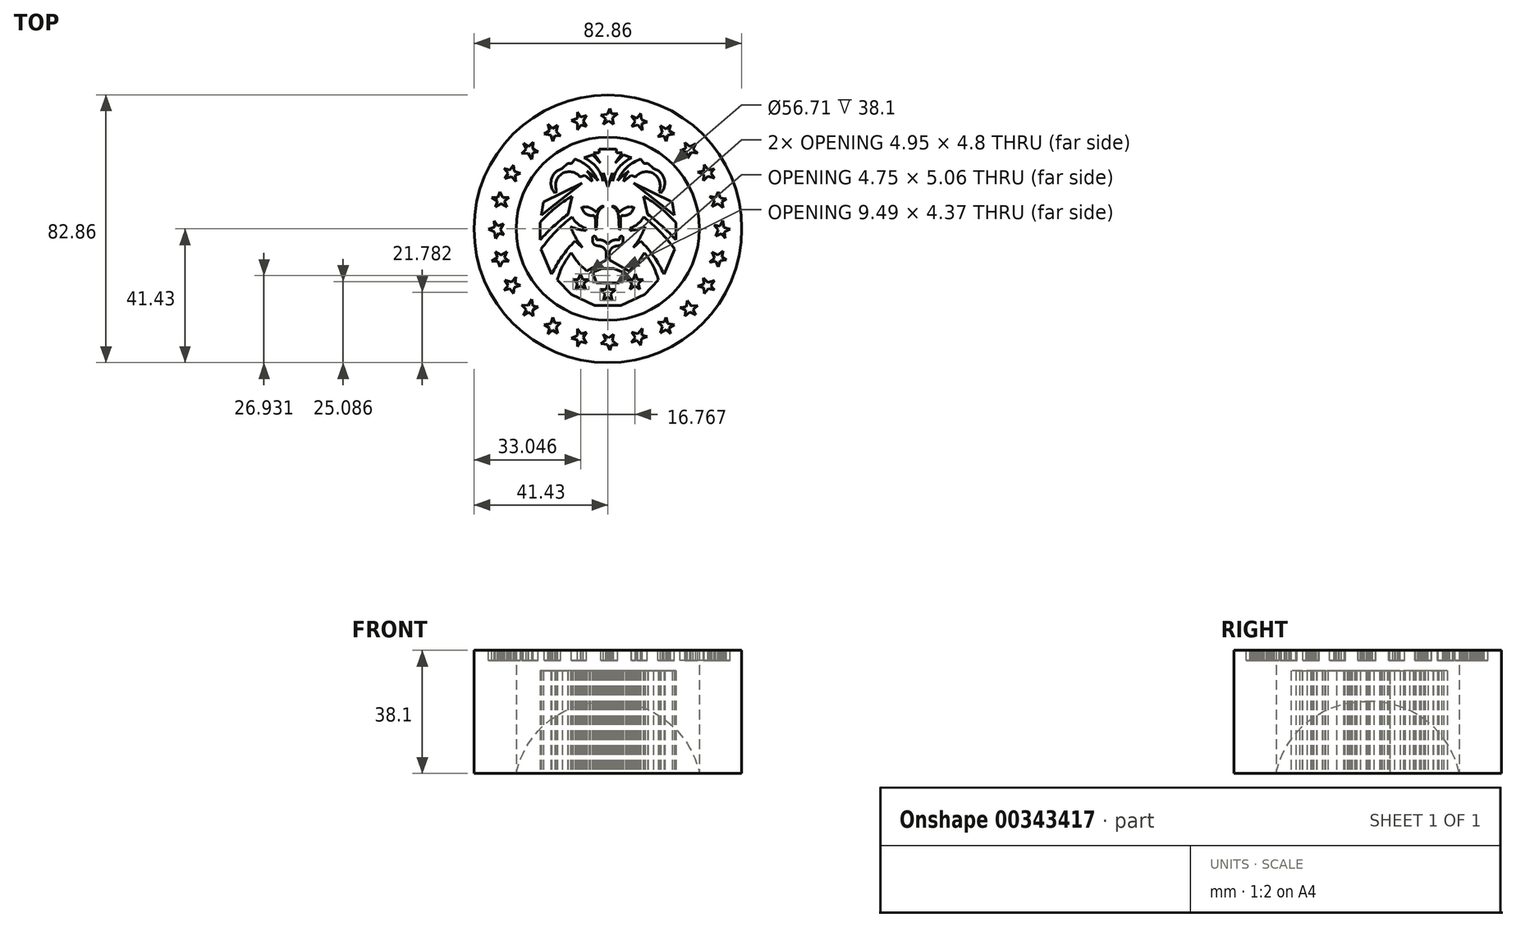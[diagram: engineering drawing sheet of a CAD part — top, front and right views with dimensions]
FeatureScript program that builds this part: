
annotation { "Feature Type Name" : "Feature", "Feature Type Description" : "" }
export const myFeature = defineFeature(function(context is Context, id is Id, definition is map)
    precondition{}
    {
        {
            var Q0;
            Q0=qCreatedBy(makeId("Top.planeOp"),FACE);
            var sketch = newSketch(context, id + "F0", { "sketchPlane" : qUnion([Q0])});
            skCircle(sketch, "E0", {"center": v(0, 0) * mm, "radius": 41.43 * mm});
            skCircle(sketch, "E1", {"center": v(0, 0) * mm, "radius": 28.35 * mm});
            skSolve(sketch);
        }
        {
            var Q0;
            Q0=qCreatedBy(makeId("Top.planeOp"),FACE);
            var sketch = newSketch(context, id + "F1", { "sketchPlane" : qUnion([Q0])});
            skLineSegment(sketch, "E2", {"start": v(0, 46.38) * mm, "end": v(0, -32.17) * mm});
            skSolve(sketch);
        }
        {
            var Q0;
            Q0=qCreatedBy(makeId("Top.planeOp"),FACE);
            var sketch = newSketch(context, id + "F2", { "sketchPlane" : qUnion([Q0])});
            skCircle(sketch, "E3", {"center": v(0, 0) * mm, "radius": 28.37 * mm});
            skSolve(sketch);
        }
        {
            var Q0;
            Q0=qCreatedBy(makeId("Top.planeOp"),FACE);
            var sketch = newSketch(context, id + "F3", { "sketchPlane" : qUnion([Q0])});
            skLineSegment(sketch, "E4", {"start": v(-11.03, 10.1) * mm, "end": v(-12.37, 4.51) * mm});
            skArc(sketch, "E5", {"start": v(-12.37, 4.51) * mm, "mid": v(-16.86, 0.72) * mm, "end": v(-21.02, -3.43) * mm});
            skLineSegment(sketch, "E6", {"start": v(-21.02, -3.43) * mm, "end": v(-21.02, 1.9) * mm});
            skArc(sketch, "E7", {"start": v(-11.03, 10.1) * mm, "mid": v(-16.36, 6.4) * mm, "end": v(-21.02, 1.9) * mm});
            skLineSegment(sketch, "E8", {"start": v(-8.04, 14.18) * mm, "end": v(-20.52, 4.22) * mm});
            skLineSegment(sketch, "E9", {"start": v(-20.52, 4.22) * mm, "end": v(-19.93, 8.27) * mm});
            skLineSegment(sketch, "E10", {"start": v(-19.93, 8.27) * mm, "end": v(-8.04, 14.18) * mm});
            skLineSegment(sketch, "E11", {"start": v(-17.38, -14.1) * mm, "end": v(-20.66, -6.3) * mm});
            skArc(sketch, "E12", {"start": v(-11.1, 3.65) * mm, "mid": v(-16.25, -0.98) * mm, "end": v(-20.66, -6.3) * mm});
            skArc(sketch, "E13", {"start": v(-11.1, 3.65) * mm, "mid": v(-9.28, 1.5) * mm, "end": v(-6.8, 0.15) * mm});
            skLineSegment(sketch, "E14", {"start": v(-6.8, 0.15) * mm, "end": v(-6.8, -0.48) * mm});
            skArc(sketch, "E15", {"start": v(-11.53, 0.68) * mm, "mid": v(-9.22, -0.13) * mm, "end": v(-6.8, -0.48) * mm});
            skArc(sketch, "E16", {"start": v(-11.53, 0.68) * mm, "mid": v(-9.97, -2.72) * mm, "end": v(-7.84, -5.8) * mm});
            skArc(sketch, "E17", {"start": v(-10.12, -3.78) * mm, "mid": v(-9, -4.81) * mm, "end": v(-7.84, -5.8) * mm});
            skArc(sketch, "E18", {"start": v(-10.12, -3.78) * mm, "mid": v(-14.22, -8.6) * mm, "end": v(-17.38, -14.1) * mm});
            skLineSegment(sketch, "E19", {"start": v(-3.6, -0.3) * mm, "end": v(-3.87, -0.1) * mm});
            skLineSegment(sketch, "E20", {"start": v(-3.87, -0.1) * mm, "end": v(-3.87, 2.84) * mm});
            skArc(sketch, "E21", {"start": v(-3.87, 2.84) * mm, "mid": v(-4, 3.55) * mm, "end": v(-4.34, 4.18) * mm});
            skArc(sketch, "E22", {"start": v(-7.84, 6.13) * mm, "mid": v(-6.5, 4.44) * mm, "end": v(-4.34, 4.18) * mm});
            skArc(sketch, "E23", {"start": v(-7.84, 6.13) * mm, "mid": v(-8.03, 6.34) * mm, "end": v(-8.3, 6.43) * mm});
            skArc(sketch, "E24", {"start": v(-5.4, 6.43) * mm, "mid": v(-6.85, 6.82) * mm, "end": v(-8.3, 6.43) * mm});
            skArc(sketch, "E25", {"start": v(-3.6, 5.13) * mm, "mid": v(-4.44, 5.87) * mm, "end": v(-5.4, 6.43) * mm});
            skFitSpline(sketch, "E26", {"points": [v(-3.6, 5.13) * mm, v(-3.38, 5.47) * mm, v(-3.2, 5.82) * mm, v(-2.82, 6.3) * mm, v(-2.41, 6.65) * mm, v(-1.95, 6.87) * mm, v(-1.78, 6.95) * mm, v(-1.2, 6.92) * mm], "startDerivative": vector(1.14, 2.33) * mm, "endDerivative": vector(4.24, -0.44) * mm});
            skArc(sketch, "E27", {"start": v(-1.2, 6.92) * mm, "mid": v(-2.6, 5.85) * mm, "end": v(-3.25, 4.2) * mm});
            skLineSegment(sketch, "E28", {"start": v(-3.25, 4.2) * mm, "end": v(-3.6, -0.3) * mm});
            skLineSegment(sketch, "E29", {"start": v(0, 24.6) * mm, "end": v(-2.68, 24.6) * mm});
            skLineSegment(sketch, "E30", {"start": v(-2.68, 24.6) * mm, "end": v(-2.68, 23.55) * mm});
            skLineSegment(sketch, "E31", {"start": v(-2.68, 23.55) * mm, "end": v(-4.43, 23.55) * mm});
            skLineSegment(sketch, "E32", {"start": v(-4.43, 23.55) * mm, "end": v(-2.25, 20.31) * mm});
            skLineSegment(sketch, "E33", {"start": v(-2.25, 20.31) * mm, "end": v(-4.76, 22.93) * mm});
            skLineSegment(sketch, "E34", {"start": v(-4.76, 22.93) * mm, "end": v(-7.41, 21.95) * mm});
            skArc(sketch, "E35", {"start": v(-1.52, 14.8) * mm, "mid": v(-3.57, 19.11) * mm, "end": v(-7.41, 21.95) * mm});
            skLineSegment(sketch, "E36", {"start": v(-1.52, 14.8) * mm, "end": v(-1.37, 17.25) * mm});
            skLineSegment(sketch, "E37", {"start": v(-1.37, 17.25) * mm, "end": v(0, 13) * mm});
            skLineSegment(sketch, "E38", {"start": v(0, 13) * mm, "end": v(0, 24.6) * mm});
            skLineSegment(sketch, "E39", {"start": v(-10.2, 21.56) * mm, "end": v(-11.2, 20.25) * mm});
            skLineSegment(sketch, "E40", {"start": v(-11.2, 20.25) * mm, "end": v(-12.45, 20.17) * mm});
            skLineSegment(sketch, "E41", {"start": v(-12.45, 20.17) * mm, "end": v(-14.05, 18.63) * mm});
            skArc(sketch, "E42", {"start": v(-14.05, 18.63) * mm, "mid": v(-17.41, 15.55) * mm, "end": v(-16.41, 11.1) * mm});
            skArc(sketch, "E43", {"start": v(-15.8, 11.64) * mm, "mid": v(-14.17, 17.04) * mm, "end": v(-8.61, 16.05) * mm});
            skLineSegment(sketch, "E44", {"start": v(-16.41, 11.1) * mm, "end": v(-15.8, 11.64) * mm});
            skLineSegment(sketch, "E45", {"start": v(-8.61, 16.05) * mm, "end": v(-7.18, 16.53) * mm});
            skLineSegment(sketch, "E46", {"start": v(-7.18, 16.53) * mm, "end": v(-4.87, 14.64) * mm});
            skArc(sketch, "E47", {"start": v(-4.87, 14.64) * mm, "mid": v(-5.43, 16.36) * mm, "end": v(-6.49, 17.82) * mm});
            skArc(sketch, "E48", {"start": v(-3.1, 14.92) * mm, "mid": v(-4.7, 16.46) * mm, "end": v(-6.49, 17.82) * mm});
            skArc(sketch, "E49", {"start": v(-3.1, 14.92) * mm, "mid": v(-5.9, 19.03) * mm, "end": v(-10.2, 21.56) * mm});
            skArc(sketch, "E50", {"start": v(0, -4.76) * mm, "mid": v(-1.62, -3.57) * mm, "end": v(-3.63, -3.45) * mm});
            skLineSegment(sketch, "E51", {"start": v(-3.63, -3.45) * mm, "end": v(-3.63, -2.82) * mm});
            skArc(sketch, "E52", {"start": v(-3.63, -2.82) * mm, "mid": v(-4.18, -2.26) * mm, "end": v(-4.74, -2.82) * mm});
            skLineSegment(sketch, "E53", {"start": v(-4.74, -2.82) * mm, "end": v(-4.74, -4.03) * mm});
            skArc(sketch, "E54", {"start": v(-4.74, -4.03) * mm, "mid": v(-4.04, -4.97) * mm, "end": v(-2.9, -5.27) * mm});
            skArc(sketch, "E55", {"start": v(-0.5, -7.1) * mm, "mid": v(-1.45, -5.86) * mm, "end": v(-2.9, -5.27) * mm});
            skLineSegment(sketch, "E56", {"start": v(-0.5, -7.1) * mm, "end": v(-0.5, -9.58) * mm});
            skLineSegment(sketch, "E57", {"start": v(-0.5, -9.58) * mm, "end": v(-6.45, -13.06) * mm});
            skArc(sketch, "E58", {"start": v(-11.28, -7.43) * mm, "mid": v(-9.16, -10.5) * mm, "end": v(-6.45, -13.06) * mm});
            skArc(sketch, "E59", {"start": v(-11.28, -7.43) * mm, "mid": v(-13.93, -11.4) * mm, "end": v(-15.65, -15.87) * mm});
            skLineSegment(sketch, "E60", {"start": v(-15.65, -15.87) * mm, "end": v(-11.37, -20.3) * mm});
            skLineSegment(sketch, "E61", {"start": v(-11.37, -20.3) * mm, "end": v(-4.05, -23.74) * mm});
            skLineSegment(sketch, "E62", {"start": v(-4.05, -23.74) * mm, "end": v(0, -23.74) * mm});
            skLineSegment(sketch, "E63", {"start": v(0, -23.74) * mm, "end": v(0, -21.12) * mm});
            skLineSegment(sketch, "E64", {"start": v(0, -21.12) * mm, "end": v(-1.36, -22.18) * mm});
            skLineSegment(sketch, "E65", {"start": v(-1.36, -22.18) * mm, "end": v(-0.9, -20.14) * mm});
            skLineSegment(sketch, "E66", {"start": v(-0.9, -20.14) * mm, "end": v(-2.38, -18.8) * mm});
            skLineSegment(sketch, "E67", {"start": v(-2.38, -18.8) * mm, "end": v(-0.55, -18.8) * mm});
            skLineSegment(sketch, "E68", {"start": v(-0.55, -18.8) * mm, "end": v(0, -17.12) * mm});
            skLineSegment(sketch, "E69", {"start": v(0, -17.12) * mm, "end": v(0, -16.68) * mm});
            skLineSegment(sketch, "E70", {"start": v(0, -16.68) * mm, "end": v(-3.54, -16.68) * mm});
            skLineSegment(sketch, "E71", {"start": v(-3.54, -16.68) * mm, "end": v(-4.74, -13.38) * mm});
            skLineSegment(sketch, "E72", {"start": v(-4.74, -13.38) * mm, "end": v(-1.8, -12.31) * mm});
            skLineSegment(sketch, "E73", {"start": v(-1.8, -12.31) * mm, "end": v(0, -12.31) * mm});
            skLineSegment(sketch, "E74", {"start": v(0, -12.31) * mm, "end": v(0, -4.76) * mm});
            skLineSegment(sketch, "E75", {"start": v(-8.46, -13.94) * mm, "end": v(-7.8, -15.72) * mm});
            skLineSegment(sketch, "E76", {"start": v(-7.8, -15.72) * mm, "end": v(-5.9, -15.72) * mm});
            skLineSegment(sketch, "E77", {"start": v(-5.9, -15.72) * mm, "end": v(-7.47, -16.87) * mm});
            skLineSegment(sketch, "E78", {"start": v(-7.47, -16.87) * mm, "end": v(-6.9, -18.73) * mm});
            skLineSegment(sketch, "E79", {"start": v(-6.9, -18.73) * mm, "end": v(-8.39, -17.6) * mm});
            skLineSegment(sketch, "E80", {"start": v(-8.39, -17.6) * mm, "end": v(-9.9, -18.74) * mm});
            skLineSegment(sketch, "E81", {"start": v(-9.9, -18.74) * mm, "end": v(-9.35, -16.93) * mm});
            skLineSegment(sketch, "E82", {"start": v(-9.35, -16.93) * mm, "end": v(-10.86, -15.77) * mm});
            skLineSegment(sketch, "E83", {"start": v(-10.86, -15.77) * mm, "end": v(-9.12, -15.77) * mm});
            skLineSegment(sketch, "E84", {"start": v(-9.12, -15.77) * mm, "end": v(-8.46, -13.94) * mm});
            skLineSegment(sketch, "E85.MirrorCS", {"start": v(0, 24.6) * mm, "end": v(2.68, 24.6) * mm});
            skLineSegment(sketch, "E86.MirrorCS", {"start": v(2.68, 24.6) * mm, "end": v(2.68, 23.55) * mm});
            skLineSegment(sketch, "E87.MirrorCS", {"start": v(2.68, 23.55) * mm, "end": v(4.43, 23.55) * mm});
            skLineSegment(sketch, "E88.MirrorCS", {"start": v(4.43, 23.55) * mm, "end": v(2.25, 20.31) * mm});
            skLineSegment(sketch, "E89.MirrorCS", {"start": v(2.25, 20.31) * mm, "end": v(4.76, 22.93) * mm});
            skLineSegment(sketch, "E90.MirrorCS", {"start": v(4.76, 22.93) * mm, "end": v(7.41, 21.95) * mm});
            skArc(sketch, "E91.MirrorCS", {"start": v(1.52, 14.8) * mm, "mid": v(3.57, 19.11) * mm, "end": v(7.41, 21.95) * mm});
            skLineSegment(sketch, "E92.MirrorCS", {"start": v(1.52, 14.8) * mm, "end": v(1.37, 17.25) * mm});
            skLineSegment(sketch, "E93.MirrorCS", {"start": v(1.37, 17.25) * mm, "end": v(0, 13) * mm});
            skArc(sketch, "E94.MirrorCS", {"start": v(3.1, 14.92) * mm, "mid": v(5.9, 19.03) * mm, "end": v(10.2, 21.56) * mm});
            skLineSegment(sketch, "E95.MirrorCS", {"start": v(10.2, 21.56) * mm, "end": v(11.2, 20.25) * mm});
            skLineSegment(sketch, "E96.MirrorCS", {"start": v(11.2, 20.25) * mm, "end": v(12.45, 20.17) * mm});
            skLineSegment(sketch, "E97.MirrorCS", {"start": v(12.45, 20.17) * mm, "end": v(14.05, 18.63) * mm});
            skArc(sketch, "E98.MirrorCS", {"start": v(14.05, 18.63) * mm, "mid": v(17.41, 15.55) * mm, "end": v(16.41, 11.1) * mm});
            skLineSegment(sketch, "E99.MirrorCS", {"start": v(16.41, 11.1) * mm, "end": v(15.8, 11.64) * mm});
            skArc(sketch, "E100.MirrorCS", {"start": v(15.8, 11.64) * mm, "mid": v(14.17, 17.04) * mm, "end": v(8.61, 16.05) * mm});
            skLineSegment(sketch, "E101.MirrorCS", {"start": v(8.61, 16.05) * mm, "end": v(7.18, 16.53) * mm});
            skLineSegment(sketch, "E102.MirrorCS", {"start": v(7.18, 16.53) * mm, "end": v(4.87, 14.64) * mm});
            skArc(sketch, "E103.MirrorCS", {"start": v(4.87, 14.64) * mm, "mid": v(5.43, 16.36) * mm, "end": v(6.49, 17.82) * mm});
            skArc(sketch, "E104.MirrorCS", {"start": v(3.1, 14.92) * mm, "mid": v(4.7, 16.46) * mm, "end": v(6.49, 17.82) * mm});
            skLineSegment(sketch, "E105.MirrorCS", {"start": v(19.93, 8.27) * mm, "end": v(8.04, 14.18) * mm});
            skLineSegment(sketch, "E106.MirrorCS", {"start": v(20.52, 4.22) * mm, "end": v(19.93, 8.27) * mm});
            skLineSegment(sketch, "E107.MirrorCS", {"start": v(8.04, 14.18) * mm, "end": v(20.52, 4.22) * mm});
            skLineSegment(sketch, "E108.MirrorCS", {"start": v(11.03, 10.1) * mm, "end": v(12.37, 4.51) * mm});
            skArc(sketch, "E109.MirrorCS", {"start": v(11.03, 10.1) * mm, "mid": v(16.36, 6.4) * mm, "end": v(21.02, 1.9) * mm});
            skLineSegment(sketch, "E110.MirrorCS", {"start": v(21.02, -3.43) * mm, "end": v(21.02, 1.9) * mm});
            skArc(sketch, "E111.MirrorCS", {"start": v(12.37, 4.51) * mm, "mid": v(16.86, 0.72) * mm, "end": v(21.02, -3.43) * mm});
            skArc(sketch, "E112.MirrorCS", {"start": v(11.1, 3.65) * mm, "mid": v(9.28, 1.5) * mm, "end": v(6.8, 0.15) * mm});
            skArc(sketch, "E113.MirrorCS", {"start": v(11.1, 3.65) * mm, "mid": v(16.25, -0.98) * mm, "end": v(20.66, -6.3) * mm});
            skLineSegment(sketch, "E114.MirrorCS", {"start": v(17.38, -14.1) * mm, "end": v(20.66, -6.3) * mm});
            skArc(sketch, "E115.MirrorCS", {"start": v(10.12, -3.78) * mm, "mid": v(14.22, -8.6) * mm, "end": v(17.38, -14.1) * mm});
            skArc(sketch, "E116.MirrorCS", {"start": v(10.12, -3.78) * mm, "mid": v(9, -4.81) * mm, "end": v(7.84, -5.8) * mm});
            skArc(sketch, "E117.MirrorCS", {"start": v(11.53, 0.68) * mm, "mid": v(9.97, -2.72) * mm, "end": v(7.84, -5.8) * mm});
            skArc(sketch, "E118.MirrorCS", {"start": v(11.53, 0.68) * mm, "mid": v(9.22, -0.13) * mm, "end": v(6.8, -0.48) * mm});
            skLineSegment(sketch, "E119.MirrorCS", {"start": v(6.8, 0.15) * mm, "end": v(6.8, -0.48) * mm});
            skFitSpline(sketch, "E120.MirrorCS", {"points": [v(3.6, 5.13) * mm, v(3.38, 5.47) * mm, v(3.2, 5.82) * mm, v(2.82, 6.3) * mm, v(2.41, 6.65) * mm, v(1.95, 6.87) * mm, v(1.78, 6.95) * mm, v(1.2, 6.92) * mm], "startDerivative": vector(-1.14, 2.33) * mm, "endDerivative": vector(-4.24, -0.44) * mm});
            skArc(sketch, "E121.MirrorCS", {"start": v(3.6, 5.13) * mm, "mid": v(4.44, 5.87) * mm, "end": v(5.4, 6.43) * mm});
            skArc(sketch, "E122.MirrorCS", {"start": v(5.4, 6.43) * mm, "mid": v(6.85, 6.82) * mm, "end": v(8.3, 6.43) * mm});
            skArc(sketch, "E123.MirrorCS", {"start": v(7.84, 6.13) * mm, "mid": v(8.03, 6.34) * mm, "end": v(8.3, 6.43) * mm});
            skArc(sketch, "E124.MirrorCS", {"start": v(7.84, 6.13) * mm, "mid": v(6.5, 4.44) * mm, "end": v(4.34, 4.18) * mm});
            skArc(sketch, "E125.MirrorCS", {"start": v(3.87, 2.84) * mm, "mid": v(4, 3.55) * mm, "end": v(4.34, 4.18) * mm});
            skLineSegment(sketch, "E126.MirrorCS", {"start": v(3.87, -0.1) * mm, "end": v(3.87, 2.84) * mm});
            skLineSegment(sketch, "E127.MirrorCS", {"start": v(3.6, -0.3) * mm, "end": v(3.87, -0.1) * mm});
            skLineSegment(sketch, "E128.MirrorCS", {"start": v(3.25, 4.2) * mm, "end": v(3.6, -0.3) * mm});
            skArc(sketch, "E129.MirrorCS", {"start": v(1.2, 6.92) * mm, "mid": v(2.6, 5.85) * mm, "end": v(3.25, 4.2) * mm});
            skArc(sketch, "E130.MirrorCS", {"start": v(0, -4.76) * mm, "mid": v(1.62, -3.57) * mm, "end": v(3.63, -3.45) * mm});
            skLineSegment(sketch, "E131.MirrorCS", {"start": v(3.63, -3.45) * mm, "end": v(3.63, -2.82) * mm});
            skArc(sketch, "E132.MirrorCS", {"start": v(3.63, -2.82) * mm, "mid": v(4.18, -2.26) * mm, "end": v(4.74, -2.82) * mm});
            skLineSegment(sketch, "E133.MirrorCS", {"start": v(4.74, -2.82) * mm, "end": v(4.74, -4.03) * mm});
            skArc(sketch, "E134.MirrorCS", {"start": v(4.74, -4.03) * mm, "mid": v(4.04, -4.97) * mm, "end": v(2.9, -5.27) * mm});
            skArc(sketch, "E135.MirrorCS", {"start": v(0.5, -7.1) * mm, "mid": v(1.45, -5.86) * mm, "end": v(2.9, -5.27) * mm});
            skLineSegment(sketch, "E136.MirrorCS", {"start": v(0.5, -7.1) * mm, "end": v(0.5, -9.58) * mm});
            skLineSegment(sketch, "E137.MirrorCS", {"start": v(0.5, -9.58) * mm, "end": v(6.45, -13.06) * mm});
            skArc(sketch, "E138.MirrorCS", {"start": v(11.28, -7.43) * mm, "mid": v(9.16, -10.5) * mm, "end": v(6.45, -13.06) * mm});
            skArc(sketch, "E139.MirrorCS", {"start": v(11.28, -7.43) * mm, "mid": v(13.93, -11.4) * mm, "end": v(15.65, -15.87) * mm});
            skLineSegment(sketch, "E140.MirrorCS", {"start": v(15.65, -15.87) * mm, "end": v(11.37, -20.3) * mm});
            skLineSegment(sketch, "E141.MirrorCS", {"start": v(11.37, -20.3) * mm, "end": v(4.05, -23.74) * mm});
            skLineSegment(sketch, "E142.MirrorCS", {"start": v(4.05, -23.74) * mm, "end": v(0, -23.74) * mm});
            skLineSegment(sketch, "E143.MirrorCS", {"start": v(0, -21.12) * mm, "end": v(1.36, -22.18) * mm});
            skLineSegment(sketch, "E144.MirrorCS", {"start": v(1.36, -22.18) * mm, "end": v(0.9, -20.14) * mm});
            skLineSegment(sketch, "E145.MirrorCS", {"start": v(0.9, -20.14) * mm, "end": v(2.38, -18.8) * mm});
            skLineSegment(sketch, "E146.MirrorCS", {"start": v(2.38, -18.8) * mm, "end": v(0.55, -18.8) * mm});
            skLineSegment(sketch, "E147.MirrorCS", {"start": v(0.55, -18.8) * mm, "end": v(0, -17.12) * mm});
            skLineSegment(sketch, "E148.MirrorCS", {"start": v(0, -16.68) * mm, "end": v(3.54, -16.68) * mm});
            skLineSegment(sketch, "E149.MirrorCS", {"start": v(3.54, -16.68) * mm, "end": v(4.74, -13.38) * mm});
            skLineSegment(sketch, "E150.MirrorCS", {"start": v(4.74, -13.38) * mm, "end": v(1.8, -12.31) * mm});
            skLineSegment(sketch, "E151.MirrorCS", {"start": v(1.8, -12.31) * mm, "end": v(0, -12.31) * mm});
            skLineSegment(sketch, "E152.MirrorCS", {"start": v(9.12, -15.77) * mm, "end": v(8.46, -13.94) * mm});
            skLineSegment(sketch, "E153.MirrorCS", {"start": v(10.86, -15.77) * mm, "end": v(9.12, -15.77) * mm});
            skLineSegment(sketch, "E154.MirrorCS", {"start": v(9.35, -16.93) * mm, "end": v(10.86, -15.77) * mm});
            skLineSegment(sketch, "E155.MirrorCS", {"start": v(9.9, -18.74) * mm, "end": v(9.35, -16.93) * mm});
            skLineSegment(sketch, "E156.MirrorCS", {"start": v(8.39, -17.6) * mm, "end": v(9.9, -18.74) * mm});
            skLineSegment(sketch, "E157.MirrorCS", {"start": v(6.9, -18.73) * mm, "end": v(8.39, -17.6) * mm});
            skLineSegment(sketch, "E158.MirrorCS", {"start": v(7.47, -16.87) * mm, "end": v(6.9, -18.73) * mm});
            skLineSegment(sketch, "E159.MirrorCS", {"start": v(5.9, -15.72) * mm, "end": v(7.47, -16.87) * mm});
            skLineSegment(sketch, "E160.MirrorCS", {"start": v(7.8, -15.72) * mm, "end": v(5.9, -15.72) * mm});
            skLineSegment(sketch, "E161.MirrorCS", {"start": v(8.46, -13.94) * mm, "end": v(7.8, -15.72) * mm});
            skSolve(sketch);
        }
        {
            var Q0;
            Q0=makeQuery(id+"F0.imprint","IMPRINT",FACE,{"disambiguationData":[TD([[makeQuery(id+"F0.imprint","IMPRINT",EDGE,{"derivedFrom":sQuery(id+"F0.wireOp",EDGE,"E0")}),1.0]])]});
            extrude(context, id + "F4", {"entities" : qUnion([Q0]), "depth" : 38.1 * mm});
        }
        {
            var Q0;
            Q0=makeQuery(id+"F4.opExtrude","CAP_FACE",FACE,{"disambiguationData":[OSD([sQuery(id+"F0.wireOp",EDGE,"E0"),sQuery(id+"F0.wireOp",EDGE,"E1")])],"isStart":false});
            var sketch = newSketch(context, id + "F5", { "sketchPlane" : qUnion([Q0])});
            skLineSegment(sketch, "E162", {"start": v(-33.47, 11.5) * mm, "end": v(-32.57, 9.68) * mm});
            skLineSegment(sketch, "E163", {"start": v(-32.57, 9.68) * mm, "end": v(-30.6, 9.68) * mm});
            skLineSegment(sketch, "E164", {"start": v(-30.6, 9.68) * mm, "end": v(-31.95, 8.6) * mm});
            skLineSegment(sketch, "E165", {"start": v(-31.95, 8.6) * mm, "end": v(-31.22, 6.78) * mm});
            skLineSegment(sketch, "E166", {"start": v(-31.22, 6.78) * mm, "end": v(-33.02, 7.83) * mm});
            skLineSegment(sketch, "E167", {"start": v(-33.02, 7.83) * mm, "end": v(-34.75, 6.72) * mm});
            skLineSegment(sketch, "E168", {"start": v(-34.75, 6.72) * mm, "end": v(-34.23, 8.6) * mm});
            skLineSegment(sketch, "E169", {"start": v(-34.23, 8.6) * mm, "end": v(-35.9, 9.68) * mm});
            skLineSegment(sketch, "E170", {"start": v(-35.9, 9.68) * mm, "end": v(-34, 9.68) * mm});
            skLineSegment(sketch, "E171", {"start": v(-34, 9.68) * mm, "end": v(-33.47, 11.5) * mm});
            skLineSegment(sketch, "E172", {"start": v(-29.26, 19.74) * mm, "end": v(-28.93, 17.74) * mm});
            skLineSegment(sketch, "E173", {"start": v(-28.93, 17.74) * mm, "end": v(-27.04, 17.16) * mm});
            skLineSegment(sketch, "E174", {"start": v(-27.04, 17.16) * mm, "end": v(-28.65, 16.52) * mm});
            skLineSegment(sketch, "E175", {"start": v(-28.65, 16.52) * mm, "end": v(-28.49, 14.57) * mm});
            skLineSegment(sketch, "E176", {"start": v(-28.49, 14.57) * mm, "end": v(-29.9, 16.1) * mm});
            skLineSegment(sketch, "E177", {"start": v(-29.9, 16.1) * mm, "end": v(-31.88, 15.55) * mm});
            skLineSegment(sketch, "E178", {"start": v(-31.88, 15.55) * mm, "end": v(-30.83, 17.19) * mm});
            skLineSegment(sketch, "E179", {"start": v(-30.83, 17.19) * mm, "end": v(-32.12, 18.72) * mm});
            skLineSegment(sketch, "E180", {"start": v(-32.12, 18.72) * mm, "end": v(-30.3, 18.16) * mm});
            skLineSegment(sketch, "E181", {"start": v(-30.3, 18.16) * mm, "end": v(-29.26, 19.74) * mm});
            skLineSegment(sketch, "E182.0", {"start": v(-32.12, 18.72) * mm, "end": v(-28.93, 17.74) * mm, "construction": true});
            skLineSegment(sketch, "E183.0", {"start": v(-30.83, 17.19) * mm, "end": v(-28.65, 16.52) * mm, "construction": true});
            skLineSegment(sketch, "E184", {"start": v(-23.14, 26.76) * mm, "end": v(-23.26, 24.73) * mm});
            skLineSegment(sketch, "E185", {"start": v(-23.26, 24.73) * mm, "end": v(-21.56, 23.74) * mm});
            skLineSegment(sketch, "E186", {"start": v(-21.56, 23.74) * mm, "end": v(-23.27, 23.48) * mm});
            skLineSegment(sketch, "E187", {"start": v(-23.27, 23.48) * mm, "end": v(-23.55, 21.54) * mm});
            skLineSegment(sketch, "E188", {"start": v(-23.55, 21.54) * mm, "end": v(-24.58, 23.35) * mm});
            skLineSegment(sketch, "E189", {"start": v(-24.58, 23.35) * mm, "end": v(-26.64, 23.25) * mm});
            skLineSegment(sketch, "E190", {"start": v(-26.64, 23.25) * mm, "end": v(-25.25, 24.62) * mm});
            skLineSegment(sketch, "E191", {"start": v(-25.25, 24.62) * mm, "end": v(-26.16, 26.4) * mm});
            skLineSegment(sketch, "E192", {"start": v(-26.16, 26.4) * mm, "end": v(-24.51, 25.45) * mm});
            skLineSegment(sketch, "E193", {"start": v(-24.51, 25.45) * mm, "end": v(-23.14, 26.76) * mm});
            skLineSegment(sketch, "E194.0", {"start": v(-26.16, 26.4) * mm, "end": v(-23.26, 24.73) * mm, "construction": true});
            skLineSegment(sketch, "E195.0", {"start": v(-25.25, 24.62) * mm, "end": v(-23.27, 23.48) * mm, "construction": true});
            skLineSegment(sketch, "E196", {"start": v(-15.5, 32.04) * mm, "end": v(-16.06, 30.09) * mm});
            skLineSegment(sketch, "E197", {"start": v(-16.06, 30.09) * mm, "end": v(-14.6, 28.76) * mm});
            skLineSegment(sketch, "E198", {"start": v(-14.6, 28.76) * mm, "end": v(-16.33, 28.86) * mm});
            skLineSegment(sketch, "E199", {"start": v(-16.33, 28.86) * mm, "end": v(-17.02, 27.04) * mm});
            skLineSegment(sketch, "E200", {"start": v(-17.02, 27.04) * mm, "end": v(-17.64, 29.02) * mm});
            skLineSegment(sketch, "E201", {"start": v(-17.64, 29.02) * mm, "end": v(-19.67, 29.37) * mm});
            skLineSegment(sketch, "E202", {"start": v(-19.67, 29.37) * mm, "end": v(-18.02, 30.4) * mm});
            skLineSegment(sketch, "E203", {"start": v(-18.02, 30.4) * mm, "end": v(-18.52, 32.34) * mm});
            skLineSegment(sketch, "E204", {"start": v(-18.52, 32.34) * mm, "end": v(-17.12, 31.06) * mm});
            skLineSegment(sketch, "E205", {"start": v(-17.12, 31.06) * mm, "end": v(-15.5, 32.04) * mm});
            skLineSegment(sketch, "E206.0", {"start": v(-18.02, 30.4) * mm, "end": v(-16.33, 28.86) * mm, "construction": true});
            skLineSegment(sketch, "E207.0", {"start": v(-18.52, 32.34) * mm, "end": v(-16.06, 30.09) * mm, "construction": true});
            skLineSegment(sketch, "E208", {"start": v(-6.6, 35.04) * mm, "end": v(-7.65, 33.3) * mm});
            skLineSegment(sketch, "E209", {"start": v(-7.65, 33.3) * mm, "end": v(-6.6, 31.63) * mm});
            skLineSegment(sketch, "E210", {"start": v(-6.6, 31.63) * mm, "end": v(-8.24, 32.2) * mm});
            skLineSegment(sketch, "E211", {"start": v(-8.24, 32.2) * mm, "end": v(-9.38, 30.61) * mm});
            skLineSegment(sketch, "E212", {"start": v(-9.38, 30.61) * mm, "end": v(-9.46, 32.69) * mm});
            skLineSegment(sketch, "E213", {"start": v(-9.46, 32.69) * mm, "end": v(-11.32, 33.56) * mm});
            skLineSegment(sketch, "E214", {"start": v(-11.32, 33.56) * mm, "end": v(-9.46, 34.12) * mm});
            skLineSegment(sketch, "E215", {"start": v(-9.46, 34.12) * mm, "end": v(-9.43, 36.12) * mm});
            skLineSegment(sketch, "E216", {"start": v(-9.43, 36.12) * mm, "end": v(-8.42, 34.51) * mm});
            skLineSegment(sketch, "E217", {"start": v(-8.42, 34.51) * mm, "end": v(-6.6, 35.04) * mm});
            skLineSegment(sketch, "E218.0", {"start": v(-9.43, 36.12) * mm, "end": v(-7.65, 33.3) * mm, "construction": true});
            skLineSegment(sketch, "E219.0", {"start": v(-9.46, 34.12) * mm, "end": v(-8.24, 32.2) * mm, "construction": true});
            skLineSegment(sketch, "E220", {"start": v(-2.15, 35.25) * mm, "end": v(-0.13, 35.4) * mm});
            skLineSegment(sketch, "E221", {"start": v(-0.13, 35.4) * mm, "end": v(0.61, 37.24) * mm});
            skLineSegment(sketch, "E222", {"start": v(0.61, 37.24) * mm, "end": v(1.12, 35.58) * mm});
            skLineSegment(sketch, "E223", {"start": v(1.12, 35.58) * mm, "end": v(3.07, 35.57) * mm});
            skLineSegment(sketch, "E224", {"start": v(3.07, 35.57) * mm, "end": v(1.42, 34.3) * mm});
            skLineSegment(sketch, "E225", {"start": v(1.42, 34.3) * mm, "end": v(1.8, 32.27) * mm});
            skLineSegment(sketch, "E226", {"start": v(1.8, 32.27) * mm, "end": v(0.26, 33.46) * mm});
            skLineSegment(sketch, "E227", {"start": v(0.26, 33.46) * mm, "end": v(-1.38, 32.31) * mm});
            skLineSegment(sketch, "E228", {"start": v(-1.38, 32.31) * mm, "end": v(-0.67, 34.08) * mm});
            skLineSegment(sketch, "E229", {"start": v(-0.67, 34.08) * mm, "end": v(-2.15, 35.25) * mm});
            skLineSegment(sketch, "E230.0", {"start": v(-1.38, 32.31) * mm, "end": v(-0.13, 35.4) * mm, "construction": true});
            skLineSegment(sketch, "E231.0", {"start": v(0.26, 33.46) * mm, "end": v(1.12, 35.58) * mm, "construction": true});
            skLineSegment(sketch, "E232", {"start": v(10.15, 35.76) * mm, "end": v(10.38, 33.74) * mm});
            skLineSegment(sketch, "E233", {"start": v(10.38, 33.74) * mm, "end": v(12.23, 33.06) * mm});
            skLineSegment(sketch, "E234", {"start": v(12.23, 33.06) * mm, "end": v(10.6, 32.5) * mm});
            skLineSegment(sketch, "E235", {"start": v(10.6, 32.5) * mm, "end": v(10.65, 30.55) * mm});
            skLineSegment(sketch, "E236", {"start": v(10.65, 30.55) * mm, "end": v(9.32, 32.15) * mm});
            skLineSegment(sketch, "E237", {"start": v(9.32, 32.15) * mm, "end": v(7.31, 31.7) * mm});
            skLineSegment(sketch, "E238", {"start": v(7.31, 31.7) * mm, "end": v(8.45, 33.28) * mm});
            skLineSegment(sketch, "E239", {"start": v(8.45, 33.28) * mm, "end": v(7.24, 34.88) * mm});
            skLineSegment(sketch, "E240", {"start": v(7.24, 34.88) * mm, "end": v(9.03, 34.23) * mm});
            skLineSegment(sketch, "E241", {"start": v(9.03, 34.23) * mm, "end": v(10.15, 35.76) * mm});
            skLineSegment(sketch, "E242.0", {"start": v(7.24, 34.88) * mm, "end": v(10.38, 33.74) * mm, "construction": true});
            skLineSegment(sketch, "E243.0", {"start": v(8.45, 33.28) * mm, "end": v(10.6, 32.5) * mm, "construction": true});
            skLineSegment(sketch, "E244", {"start": v(20.58, 29.39) * mm, "end": v(18.6, 28.98) * mm});
            skLineSegment(sketch, "E245", {"start": v(18.6, 28.98) * mm, "end": v(18.08, 27.07) * mm});
            skLineSegment(sketch, "E246", {"start": v(18.08, 27.07) * mm, "end": v(17.38, 28.66) * mm});
            skLineSegment(sketch, "E247", {"start": v(17.38, 28.66) * mm, "end": v(15.44, 28.43) * mm});
            skLineSegment(sketch, "E248", {"start": v(15.44, 28.43) * mm, "end": v(16.92, 29.9) * mm});
            skLineSegment(sketch, "E249", {"start": v(16.92, 29.9) * mm, "end": v(16.3, 31.85) * mm});
            skLineSegment(sketch, "E250", {"start": v(16.3, 31.85) * mm, "end": v(17.97, 30.86) * mm});
            skLineSegment(sketch, "E251", {"start": v(17.97, 30.86) * mm, "end": v(19.46, 32.2) * mm});
            skLineSegment(sketch, "E252", {"start": v(19.46, 32.2) * mm, "end": v(18.96, 30.37) * mm});
            skLineSegment(sketch, "E253", {"start": v(18.96, 30.37) * mm, "end": v(20.58, 29.39) * mm});
            skLineSegment(sketch, "E254.0", {"start": v(19.46, 32.2) * mm, "end": v(18.6, 28.98) * mm, "construction": true});
            skLineSegment(sketch, "E255.0", {"start": v(17.97, 30.86) * mm, "end": v(17.38, 28.66) * mm, "construction": true});
            skLineSegment(sketch, "E256", {"start": v(23.8, 26.74) * mm, "end": v(25.38, 25.46) * mm});
            skLineSegment(sketch, "E257", {"start": v(25.38, 25.46) * mm, "end": v(27.17, 26.26) * mm});
            skLineSegment(sketch, "E258", {"start": v(27.17, 26.26) * mm, "end": v(26.39, 24.72) * mm});
            skLineSegment(sketch, "E259", {"start": v(26.39, 24.72) * mm, "end": v(27.8, 23.36) * mm});
            skLineSegment(sketch, "E260", {"start": v(27.8, 23.36) * mm, "end": v(25.73, 23.58) * mm});
            skLineSegment(sketch, "E261", {"start": v(25.73, 23.58) * mm, "end": v(24.6, 21.86) * mm});
            skLineSegment(sketch, "E262", {"start": v(24.6, 21.86) * mm, "end": v(24.3, 23.78) * mm});
            skLineSegment(sketch, "E263", {"start": v(24.3, 23.78) * mm, "end": v(22.33, 24.09) * mm});
            skLineSegment(sketch, "E264", {"start": v(22.33, 24.09) * mm, "end": v(24.06, 24.87) * mm});
            skLineSegment(sketch, "E265", {"start": v(24.06, 24.87) * mm, "end": v(23.8, 26.74) * mm});
            skLineSegment(sketch, "E266.0", {"start": v(22.33, 24.09) * mm, "end": v(25.38, 25.46) * mm, "construction": true});
            skLineSegment(sketch, "E267.0", {"start": v(24.3, 23.78) * mm, "end": v(26.39, 24.72) * mm, "construction": true});
            skLineSegment(sketch, "E268", {"start": v(29.79, 19.77) * mm, "end": v(31.06, 18.18) * mm});
            skLineSegment(sketch, "E269", {"start": v(31.06, 18.18) * mm, "end": v(32.98, 18.6) * mm});
            skLineSegment(sketch, "E270", {"start": v(32.98, 18.6) * mm, "end": v(31.89, 17.24) * mm});
            skLineSegment(sketch, "E271", {"start": v(31.89, 17.24) * mm, "end": v(32.98, 15.62) * mm});
            skLineSegment(sketch, "E272", {"start": v(32.98, 15.62) * mm, "end": v(31, 16.27) * mm});
            skLineSegment(sketch, "E273", {"start": v(31, 16.27) * mm, "end": v(29.54, 14.83) * mm});
            skLineSegment(sketch, "E274", {"start": v(29.54, 14.83) * mm, "end": v(29.66, 16.77) * mm});
            skLineSegment(sketch, "E275", {"start": v(29.66, 16.77) * mm, "end": v(27.79, 17.49) * mm});
            skLineSegment(sketch, "E276", {"start": v(27.79, 17.49) * mm, "end": v(29.65, 17.88) * mm});
            skLineSegment(sketch, "E277", {"start": v(29.65, 17.88) * mm, "end": v(29.79, 19.77) * mm});
            skLineSegment(sketch, "E278.0", {"start": v(29.66, 16.77) * mm, "end": v(31.89, 17.24) * mm, "construction": true});
            skLineSegment(sketch, "E279.0", {"start": v(27.79, 17.49) * mm, "end": v(31.06, 18.18) * mm, "construction": true});
            skLineSegment(sketch, "E280", {"start": v(34.14, 11.46) * mm, "end": v(34.8, 9.53) * mm});
            skLineSegment(sketch, "E281", {"start": v(34.8, 9.53) * mm, "end": v(36.74, 9.26) * mm});
            skLineSegment(sketch, "E282", {"start": v(36.74, 9.26) * mm, "end": v(35.25, 8.37) * mm});
            skLineSegment(sketch, "E283", {"start": v(35.25, 8.37) * mm, "end": v(35.72, 6.47) * mm});
            skLineSegment(sketch, "E284", {"start": v(35.72, 6.47) * mm, "end": v(34.09, 7.76) * mm});
            skLineSegment(sketch, "E285", {"start": v(34.09, 7.76) * mm, "end": v(32.22, 6.9) * mm});
            skLineSegment(sketch, "E286", {"start": v(32.22, 6.9) * mm, "end": v(33, 8.68) * mm});
            skLineSegment(sketch, "E287", {"start": v(33, 8.68) * mm, "end": v(31.48, 10) * mm});
            skLineSegment(sketch, "E288", {"start": v(31.48, 10) * mm, "end": v(33.37, 9.73) * mm});
            skLineSegment(sketch, "E289", {"start": v(33.37, 9.73) * mm, "end": v(34.14, 11.46) * mm});
            skLineSegment(sketch, "E290.0", {"start": v(33, 8.68) * mm, "end": v(35.25, 8.37) * mm, "construction": true});
            skLineSegment(sketch, "E291.0", {"start": v(31.48, 10) * mm, "end": v(34.8, 9.53) * mm, "construction": true});
            skLineSegment(sketch, "E292.MirrorCS", {"start": v(-33.47, -11.84) * mm, "end": v(-32.57, -10.02) * mm});
            skLineSegment(sketch, "E293.MirrorCS", {"start": v(-32.57, -10.02) * mm, "end": v(-30.6, -10.02) * mm});
            skLineSegment(sketch, "E294.MirrorCS", {"start": v(-30.6, -10.02) * mm, "end": v(-31.95, -8.93) * mm});
            skLineSegment(sketch, "E295.MirrorCS", {"start": v(-34.75, -7.06) * mm, "end": v(-34.23, -8.93) * mm});
            skLineSegment(sketch, "E296.MirrorCS", {"start": v(-34.23, -8.93) * mm, "end": v(-35.9, -10.02) * mm});
            skLineSegment(sketch, "E297.MirrorCS", {"start": v(-35.9, -10.02) * mm, "end": v(-34, -10.02) * mm});
            skLineSegment(sketch, "E298.MirrorCS", {"start": v(-34, -10.02) * mm, "end": v(-33.47, -11.84) * mm});
            skLineSegment(sketch, "E299.MirrorCS", {"start": v(-31.95, -8.93) * mm, "end": v(-31.22, -7.12) * mm});
            skLineSegment(sketch, "E300.MirrorCS", {"start": v(-31.22, -7.12) * mm, "end": v(-33.02, -8.16) * mm});
            skLineSegment(sketch, "E301.MirrorCS", {"start": v(-33.02, -8.16) * mm, "end": v(-34.75, -7.06) * mm});
            skLineSegment(sketch, "E302.MirrorCS", {"start": v(-29.9, -16.44) * mm, "end": v(-31.88, -15.89) * mm});
            skLineSegment(sketch, "E303.MirrorCS", {"start": v(-28.49, -14.91) * mm, "end": v(-29.9, -16.44) * mm});
            skLineSegment(sketch, "E304.MirrorCS", {"start": v(-28.65, -16.86) * mm, "end": v(-28.49, -14.91) * mm});
            skLineSegment(sketch, "E305.MirrorCS", {"start": v(-27.04, -17.5) * mm, "end": v(-28.65, -16.86) * mm});
            skLineSegment(sketch, "E306.MirrorCS", {"start": v(-28.93, -18.08) * mm, "end": v(-27.04, -17.5) * mm});
            skLineSegment(sketch, "E307.MirrorCS", {"start": v(-29.26, -20.08) * mm, "end": v(-28.93, -18.08) * mm});
            skLineSegment(sketch, "E308.MirrorCS", {"start": v(-30.3, -18.5) * mm, "end": v(-29.26, -20.08) * mm});
            skLineSegment(sketch, "E309.MirrorCS", {"start": v(-32.12, -19.06) * mm, "end": v(-28.93, -18.08) * mm, "construction": true});
            skLineSegment(sketch, "E310.MirrorCS", {"start": v(-30.83, -17.52) * mm, "end": v(-32.12, -19.06) * mm});
            skLineSegment(sketch, "E311.MirrorCS", {"start": v(-31.88, -15.89) * mm, "end": v(-30.83, -17.52) * mm});
            skLineSegment(sketch, "E312.MirrorCS", {"start": v(-24.51, -25.79) * mm, "end": v(-23.14, -27.1) * mm});
            skLineSegment(sketch, "E313.MirrorCS", {"start": v(-26.16, -26.74) * mm, "end": v(-23.26, -25.07) * mm, "construction": true});
            skLineSegment(sketch, "E314.MirrorCS", {"start": v(-25.25, -24.95) * mm, "end": v(-26.16, -26.74) * mm});
            skLineSegment(sketch, "E315.MirrorCS", {"start": v(-26.64, -23.6) * mm, "end": v(-25.25, -24.95) * mm});
            skLineSegment(sketch, "E316.MirrorCS", {"start": v(-24.58, -23.69) * mm, "end": v(-26.64, -23.6) * mm});
            skLineSegment(sketch, "E317.MirrorCS", {"start": v(-23.55, -21.88) * mm, "end": v(-24.58, -23.69) * mm});
            skLineSegment(sketch, "E318.MirrorCS", {"start": v(-23.27, -23.81) * mm, "end": v(-23.55, -21.88) * mm});
            skLineSegment(sketch, "E319.MirrorCS", {"start": v(-21.56, -24.08) * mm, "end": v(-23.27, -23.81) * mm});
            skLineSegment(sketch, "E320.MirrorCS", {"start": v(-23.26, -25.07) * mm, "end": v(-21.56, -24.08) * mm});
            skLineSegment(sketch, "E321.MirrorCS", {"start": v(-23.14, -27.1) * mm, "end": v(-23.26, -25.07) * mm});
            skLineSegment(sketch, "E322.MirrorCS", {"start": v(-17.12, -31.4) * mm, "end": v(-15.5, -32.38) * mm});
            skLineSegment(sketch, "E323.MirrorCS", {"start": v(-18.52, -32.68) * mm, "end": v(-16.06, -30.43) * mm, "construction": true});
            skLineSegment(sketch, "E324.MirrorCS", {"start": v(-18.02, -30.74) * mm, "end": v(-18.52, -32.68) * mm});
            skLineSegment(sketch, "E325.MirrorCS", {"start": v(-19.67, -29.71) * mm, "end": v(-18.02, -30.74) * mm});
            skLineSegment(sketch, "E326.MirrorCS", {"start": v(-17.64, -29.36) * mm, "end": v(-19.67, -29.71) * mm});
            skLineSegment(sketch, "E327.MirrorCS", {"start": v(-17.02, -27.38) * mm, "end": v(-17.64, -29.36) * mm});
            skLineSegment(sketch, "E328.MirrorCS", {"start": v(-16.33, -29.2) * mm, "end": v(-17.02, -27.38) * mm});
            skLineSegment(sketch, "E329.MirrorCS", {"start": v(-14.6, -29.1) * mm, "end": v(-16.33, -29.2) * mm});
            skLineSegment(sketch, "E330.MirrorCS", {"start": v(-16.06, -30.43) * mm, "end": v(-14.6, -29.1) * mm});
            skLineSegment(sketch, "E331.MirrorCS", {"start": v(-15.5, -32.38) * mm, "end": v(-16.06, -30.43) * mm});
            skLineSegment(sketch, "E332.MirrorCS", {"start": v(-9.46, -34.46) * mm, "end": v(-9.43, -36.46) * mm});
            skLineSegment(sketch, "E333.MirrorCS", {"start": v(-11.32, -33.9) * mm, "end": v(-9.46, -34.46) * mm});
            skLineSegment(sketch, "E334.MirrorCS", {"start": v(-9.46, -33.03) * mm, "end": v(-11.32, -33.9) * mm});
            skLineSegment(sketch, "E335.MirrorCS", {"start": v(-9.38, -30.95) * mm, "end": v(-9.46, -33.03) * mm});
            skLineSegment(sketch, "E336.MirrorCS", {"start": v(-8.24, -32.53) * mm, "end": v(-9.38, -30.95) * mm});
            skLineSegment(sketch, "E337.MirrorCS", {"start": v(-6.6, -31.97) * mm, "end": v(-8.24, -32.53) * mm});
            skLineSegment(sketch, "E338.MirrorCS", {"start": v(-7.65, -33.64) * mm, "end": v(-6.6, -31.97) * mm});
            skLineSegment(sketch, "E339.MirrorCS", {"start": v(-6.6, -35.38) * mm, "end": v(-7.65, -33.64) * mm});
            skLineSegment(sketch, "E340.MirrorCS", {"start": v(-8.42, -34.85) * mm, "end": v(-6.6, -35.38) * mm});
            skLineSegment(sketch, "E341.MirrorCS", {"start": v(-9.43, -36.46) * mm, "end": v(-7.65, -33.64) * mm, "construction": true});
            skLineSegment(sketch, "E342.MirrorCS", {"start": v(-2.15, -35.59) * mm, "end": v(-0.13, -35.75) * mm});
            skLineSegment(sketch, "E343.MirrorCS", {"start": v(-0.67, -34.41) * mm, "end": v(-2.15, -35.59) * mm});
            skLineSegment(sketch, "E344.MirrorCS", {"start": v(-1.38, -32.65) * mm, "end": v(-0.13, -35.75) * mm, "construction": true});
            skLineSegment(sketch, "E345.MirrorCS", {"start": v(0.26, -33.8) * mm, "end": v(-1.38, -32.65) * mm});
            skLineSegment(sketch, "E346.MirrorCS", {"start": v(1.8, -32.61) * mm, "end": v(0.26, -33.8) * mm});
            skLineSegment(sketch, "E347.MirrorCS", {"start": v(1.42, -34.63) * mm, "end": v(1.8, -32.61) * mm});
            skLineSegment(sketch, "E348.MirrorCS", {"start": v(3.07, -35.9) * mm, "end": v(1.42, -34.63) * mm});
            skLineSegment(sketch, "E349.MirrorCS", {"start": v(1.12, -35.91) * mm, "end": v(3.07, -35.9) * mm});
            skLineSegment(sketch, "E350.MirrorCS", {"start": v(0.61, -37.57) * mm, "end": v(1.12, -35.91) * mm});
            skLineSegment(sketch, "E351.MirrorCS", {"start": v(-0.13, -35.75) * mm, "end": v(0.61, -37.57) * mm});
            skLineSegment(sketch, "E352.MirrorCS", {"start": v(9.03, -34.57) * mm, "end": v(10.15, -36.1) * mm});
            skLineSegment(sketch, "E353.MirrorCS", {"start": v(7.24, -35.22) * mm, "end": v(10.38, -34.08) * mm, "construction": true});
            skLineSegment(sketch, "E354.MirrorCS", {"start": v(8.45, -33.62) * mm, "end": v(7.24, -35.22) * mm});
            skLineSegment(sketch, "E355.MirrorCS", {"start": v(7.31, -32.04) * mm, "end": v(8.45, -33.62) * mm});
            skLineSegment(sketch, "E356.MirrorCS", {"start": v(9.32, -32.49) * mm, "end": v(7.31, -32.04) * mm});
            skLineSegment(sketch, "E357.MirrorCS", {"start": v(10.65, -30.9) * mm, "end": v(9.32, -32.49) * mm});
            skLineSegment(sketch, "E358.MirrorCS", {"start": v(10.6, -32.84) * mm, "end": v(10.65, -30.9) * mm});
            skLineSegment(sketch, "E359.MirrorCS", {"start": v(12.23, -33.4) * mm, "end": v(10.6, -32.84) * mm});
            skLineSegment(sketch, "E360.MirrorCS", {"start": v(10.38, -34.08) * mm, "end": v(12.23, -33.4) * mm});
            skLineSegment(sketch, "E361.MirrorCS", {"start": v(10.15, -36.1) * mm, "end": v(10.38, -34.08) * mm});
            skLineSegment(sketch, "E362.MirrorCS", {"start": v(19.46, -32.54) * mm, "end": v(18.6, -29.32) * mm, "construction": true});
            skLineSegment(sketch, "E363.MirrorCS", {"start": v(18.96, -30.7) * mm, "end": v(20.58, -29.72) * mm});
            skLineSegment(sketch, "E364.MirrorCS", {"start": v(20.58, -29.72) * mm, "end": v(18.6, -29.32) * mm});
            skLineSegment(sketch, "E365.MirrorCS", {"start": v(18.6, -29.32) * mm, "end": v(18.08, -27.41) * mm});
            skLineSegment(sketch, "E366.MirrorCS", {"start": v(18.08, -27.41) * mm, "end": v(17.38, -29) * mm});
            skLineSegment(sketch, "E367.MirrorCS", {"start": v(17.38, -29) * mm, "end": v(15.44, -28.77) * mm});
            skLineSegment(sketch, "E368.MirrorCS", {"start": v(15.44, -28.77) * mm, "end": v(16.92, -30.23) * mm});
            skLineSegment(sketch, "E369.MirrorCS", {"start": v(16.92, -30.23) * mm, "end": v(16.3, -32.2) * mm});
            skLineSegment(sketch, "E370.MirrorCS", {"start": v(16.3, -32.2) * mm, "end": v(17.97, -31.2) * mm});
            skLineSegment(sketch, "E371.MirrorCS", {"start": v(17.97, -31.2) * mm, "end": v(19.46, -32.54) * mm});
            skLineSegment(sketch, "E372.MirrorCS", {"start": v(27.17, -26.6) * mm, "end": v(26.39, -25.05) * mm});
            skLineSegment(sketch, "E373.MirrorCS", {"start": v(26.39, -25.05) * mm, "end": v(27.8, -23.7) * mm});
            skLineSegment(sketch, "E374.MirrorCS", {"start": v(27.8, -23.7) * mm, "end": v(25.73, -23.92) * mm});
            skLineSegment(sketch, "E375.MirrorCS", {"start": v(25.73, -23.92) * mm, "end": v(24.6, -22.2) * mm});
            skLineSegment(sketch, "E376.MirrorCS", {"start": v(24.6, -22.2) * mm, "end": v(24.3, -24.12) * mm});
            skLineSegment(sketch, "E377.MirrorCS", {"start": v(24.3, -24.12) * mm, "end": v(22.33, -24.43) * mm});
            skLineSegment(sketch, "E378.MirrorCS", {"start": v(22.33, -24.43) * mm, "end": v(25.38, -25.8) * mm, "construction": true});
            skLineSegment(sketch, "E379.MirrorCS", {"start": v(24.06, -25.2) * mm, "end": v(23.8, -27.08) * mm});
            skLineSegment(sketch, "E380.MirrorCS", {"start": v(23.8, -27.08) * mm, "end": v(25.38, -25.8) * mm});
            skLineSegment(sketch, "E381.MirrorCS", {"start": v(25.38, -25.8) * mm, "end": v(27.17, -26.6) * mm});
            skLineSegment(sketch, "E382.MirrorCS", {"start": v(32.98, -18.93) * mm, "end": v(31.89, -17.58) * mm});
            skLineSegment(sketch, "E383.MirrorCS", {"start": v(31.89, -17.58) * mm, "end": v(32.98, -15.96) * mm});
            skLineSegment(sketch, "E384.MirrorCS", {"start": v(32.98, -15.96) * mm, "end": v(31, -16.61) * mm});
            skLineSegment(sketch, "E385.MirrorCS", {"start": v(31, -16.61) * mm, "end": v(29.54, -15.17) * mm});
            skLineSegment(sketch, "E386.MirrorCS", {"start": v(29.54, -15.17) * mm, "end": v(29.66, -17.1) * mm});
            skLineSegment(sketch, "E387.MirrorCS", {"start": v(29.66, -17.1) * mm, "end": v(27.79, -17.82) * mm});
            skLineSegment(sketch, "E388.MirrorCS", {"start": v(27.79, -17.82) * mm, "end": v(31.06, -18.52) * mm, "construction": true});
            skLineSegment(sketch, "E389.MirrorCS", {"start": v(29.65, -18.22) * mm, "end": v(29.79, -20.1) * mm});
            skLineSegment(sketch, "E390.MirrorCS", {"start": v(29.79, -20.1) * mm, "end": v(31.06, -18.52) * mm});
            skLineSegment(sketch, "E391.MirrorCS", {"start": v(31.06, -18.52) * mm, "end": v(32.98, -18.93) * mm});
            skLineSegment(sketch, "E392.MirrorCS", {"start": v(36.74, -9.6) * mm, "end": v(35.25, -8.7) * mm});
            skLineSegment(sketch, "E393.MirrorCS", {"start": v(35.25, -8.7) * mm, "end": v(35.72, -6.81) * mm});
            skLineSegment(sketch, "E394.MirrorCS", {"start": v(35.72, -6.81) * mm, "end": v(34.09, -8.1) * mm});
            skLineSegment(sketch, "E395.MirrorCS", {"start": v(34.09, -8.1) * mm, "end": v(32.22, -7.24) * mm});
            skLineSegment(sketch, "E396.MirrorCS", {"start": v(32.22, -7.24) * mm, "end": v(33, -9.02) * mm});
            skLineSegment(sketch, "E397.MirrorCS", {"start": v(33, -9.02) * mm, "end": v(31.48, -10.33) * mm});
            skLineSegment(sketch, "E398.MirrorCS", {"start": v(31.48, -10.33) * mm, "end": v(34.8, -9.87) * mm, "construction": true});
            skLineSegment(sketch, "E399.MirrorCS", {"start": v(33.37, -10.07) * mm, "end": v(34.14, -11.8) * mm});
            skLineSegment(sketch, "E400.MirrorCS", {"start": v(34.14, -11.8) * mm, "end": v(34.8, -9.87) * mm});
            skLineSegment(sketch, "E401.MirrorCS", {"start": v(34.8, -9.87) * mm, "end": v(36.74, -9.6) * mm});
            skLineSegment(sketch, "E402", {"start": v(-32.3, 1.53) * mm, "end": v(-33.27, -0.26) * mm});
            skLineSegment(sketch, "E403", {"start": v(-33.27, -0.26) * mm, "end": v(-32.14, -1.87) * mm});
            skLineSegment(sketch, "E404", {"start": v(-32.14, -1.87) * mm, "end": v(-33.8, -1.4) * mm});
            skLineSegment(sketch, "E405", {"start": v(-33.8, -1.4) * mm, "end": v(-34.87, -3.03) * mm});
            skLineSegment(sketch, "E406", {"start": v(-34.87, -3.03) * mm, "end": v(-35.05, -0.95) * mm});
            skLineSegment(sketch, "E407", {"start": v(-35.05, -0.95) * mm, "end": v(-36.95, -0.17) * mm});
            skLineSegment(sketch, "E408", {"start": v(-36.95, -0.17) * mm, "end": v(-35.11, 0.48) * mm});
            skLineSegment(sketch, "E409", {"start": v(-35.11, 0.48) * mm, "end": v(-35.18, 2.48) * mm});
            skLineSegment(sketch, "E410", {"start": v(-35.18, 2.48) * mm, "end": v(-34.1, 0.92) * mm});
            skLineSegment(sketch, "E411", {"start": v(-34.1, 0.92) * mm, "end": v(-32.3, 1.53) * mm});
            skLineSegment(sketch, "E412.0", {"start": v(-35.18, 2.48) * mm, "end": v(-33.27, -0.26) * mm, "construction": true});
            skLineSegment(sketch, "E413.0", {"start": v(-35.11, 0.48) * mm, "end": v(-33.8, -1.4) * mm, "construction": true});
            skLineSegment(sketch, "E414", {"start": v(33.37, -2.27) * mm, "end": v(34.18, -0.4) * mm});
            skLineSegment(sketch, "E415", {"start": v(34.18, -0.4) * mm, "end": v(32.92, 1.1) * mm});
            skLineSegment(sketch, "E416", {"start": v(32.92, 1.1) * mm, "end": v(34.62, 0.77) * mm});
            skLineSegment(sketch, "E417", {"start": v(34.62, 0.77) * mm, "end": v(35.54, 2.5) * mm});
            skLineSegment(sketch, "E418", {"start": v(35.54, 2.5) * mm, "end": v(35.9, 0.45) * mm});
            skLineSegment(sketch, "E419", {"start": v(35.9, 0.45) * mm, "end": v(37.86, -0.17) * mm});
            skLineSegment(sketch, "E420", {"start": v(37.86, -0.17) * mm, "end": v(36.08, -0.97) * mm});
            skLineSegment(sketch, "E421", {"start": v(36.08, -0.97) * mm, "end": v(36.33, -2.96) * mm});
            skLineSegment(sketch, "E422", {"start": v(36.33, -2.96) * mm, "end": v(35.1, -1.5) * mm});
            skLineSegment(sketch, "E423", {"start": v(35.1, -1.5) * mm, "end": v(33.37, -2.27) * mm});
            skLineSegment(sketch, "E424.0", {"start": v(36.33, -2.96) * mm, "end": v(34.18, -0.4) * mm, "construction": true});
            skLineSegment(sketch, "E425.0", {"start": v(36.08, -0.97) * mm, "end": v(34.62, 0.77) * mm, "construction": true});
            skLineSegment(sketch, "E426", {"start": v(-30.3, -18.5) * mm, "end": v(-32.12, -19.06) * mm});
            skLineSegment(sketch, "E427", {"start": v(-24.51, -25.79) * mm, "end": v(-26.16, -26.74) * mm});
            skLineSegment(sketch, "E428", {"start": v(-18.52, -32.68) * mm, "end": v(-17.12, -31.4) * mm});
            skLineSegment(sketch, "E429", {"start": v(-8.42, -34.85) * mm, "end": v(-9.43, -36.46) * mm});
            skLineSegment(sketch, "E430", {"start": v(-0.67, -34.41) * mm, "end": v(-1.38, -32.65) * mm});
            skLineSegment(sketch, "E431", {"start": v(9.03, -34.57) * mm, "end": v(7.24, -35.22) * mm});
            skLineSegment(sketch, "E432", {"start": v(18.96, -30.7) * mm, "end": v(19.46, -32.54) * mm});
            skLineSegment(sketch, "E433", {"start": v(24.06, -25.2) * mm, "end": v(22.33, -24.43) * mm});
            skLineSegment(sketch, "E434", {"start": v(29.65, -18.22) * mm, "end": v(27.79, -17.82) * mm});
            skLineSegment(sketch, "E435", {"start": v(33.37, -10.07) * mm, "end": v(31.48, -10.33) * mm});
            skSolve(sketch);
        }
        {
            var Q0;
            Q0 = qSketchRegion(id + "F5", true);
            extrude(context, id + "F6", {"entities" : qUnion([Q0]), "operationType" : NewBodyOperationType.REMOVE, "oppositeDirection" : true, "depth" : 3.17 * mm});
        }
        {
            var Q0;
            Q0 = qSketchRegion(id + "F3", true);
            extrude(context, id + "F7", {"entities" : qUnion([Q0]), "depth" : 31.75 * mm});
        }
        {
            var Q0;
            Q0 = qSketchRegion(id + "F2", true);
            extrude(context, id + "F8", {"entities" : qUnion([Q0]), "depth" : 22.22 * mm});
        }
        {
            var Q0;
            Q0=makeQuery(id+"F8.opExtrude","CAP_EDGE",EDGE,{"disambiguationData":[OSD([sQuery(id+"F2.wireOp",EDGE,"E3")])],"isStart":false});
            fillet(context, id + "F9", {"entities" : qUnion([Q0]), "radius" : 28.17 * mm, "tangentPropagation" : true, "allowEdgeOverflow" : false});
        }
    });
